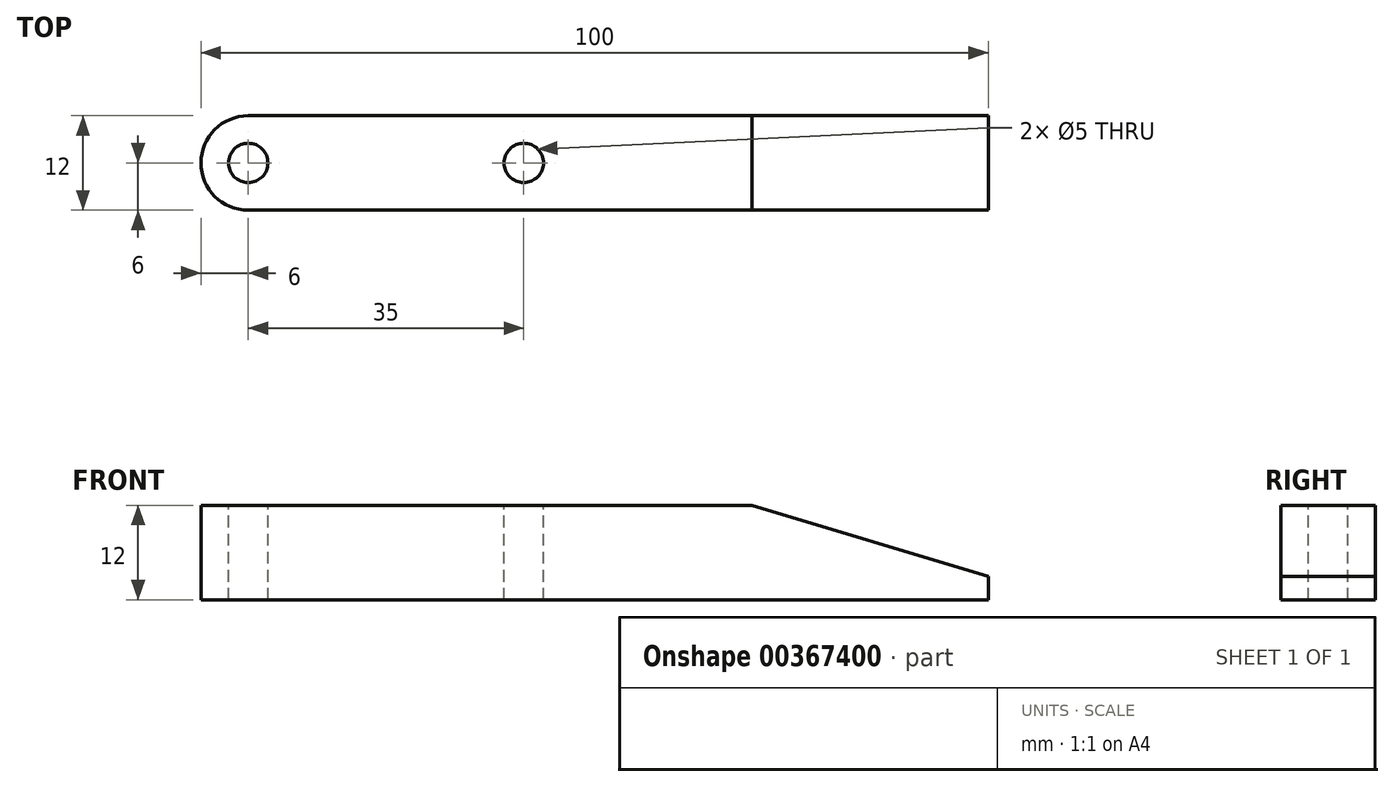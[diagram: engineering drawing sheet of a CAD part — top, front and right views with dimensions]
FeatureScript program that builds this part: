
annotation { "Feature Type Name" : "Feature", "Feature Type Description" : "" }
export const myFeature = defineFeature(function(context is Context, id is Id, definition is map)
    precondition{}
    {
        {
            var Q0;
            Q0=qCreatedBy(makeId("Top.planeOp"),FACE);
            var sketch = newSketch(context, id + "F0", { "sketchPlane" : qUnion([Q0])});
            skLineSegment(sketch, "E0.bottom", {"start": v(0, 0) * mm, "end": v(100, 0) * mm});
            skLineSegment(sketch, "E0.top", {"start": v(0, 12) * mm, "end": v(100, 12) * mm});
            skLineSegment(sketch, "E0.left", {"start": v(0, 0) * mm, "end": v(0, 12) * mm});
            skLineSegment(sketch, "E0.right", {"start": v(100, 0) * mm, "end": v(100, 12) * mm});
            skSolve(sketch);
        }
        {
            var Q0;
            Q0=makeQuery(id+"F0.imprint","IMPRINT",FACE,{"disambiguationData":[TD([[makeQuery(id+"F0.imprint","IMPRINT",EDGE,{"derivedFrom":sQuery(id+"F0.wireOp",EDGE,"E0.bottom")}),1.0]])]});
            extrude(context, id + "F1", {"entities" : qUnion([Q0]), "depth" : 12 * mm});
        }
        {
            var Q0;
            Q0=makeQuery(id+"F1.opExtrude","CAP_EDGE",EDGE,{"disambiguationData":[OSD([sQuery(id+"F0.wireOp",EDGE,"E0.right")])],"isStart":false});
            chamfer(context, id + "F2", {"entities" : qUnion([Q0]), "chamferType" : ChamferType.TWO_OFFSETS, "width1" : 30 * mm, "oppositeDirection" : false, "width2" : 9 * mm, "tangentPropagation" : true});
        }
        {
            var Q0;
            Q0=makeQuery(id+"F1.opExtrude","SWEPT_EDGE",EDGE,{"disambiguationData":[OSD([sQuery(id+"F0.wireOp",EDGE,"E0.bottom"),sQuery(id+"F0.wireOp",EDGE,"E0.left")])]});
            var Q1;
            Q1=makeQuery(id+"F1.opExtrude","SWEPT_EDGE",EDGE,{"disambiguationData":[OSD([sQuery(id+"F0.wireOp",EDGE,"E0.top"),sQuery(id+"F0.wireOp",EDGE,"E0.left")])]});
            fillet(context, id + "F3", {"entities" : qUnion([Q0, Q1]), "radius" : 6 * mm, "tangentPropagation" : true, "allowEdgeOverflow" : false});
        }
        {
            var Q0;
            Q0=makeQuery(id+"F1.opExtrude","CAP_FACE",FACE,{"disambiguationData":[OSD([sQuery(id+"F0.wireOp",EDGE,"E0.bottom"),sQuery(id+"F0.wireOp",EDGE,"E0.top"),sQuery(id+"F0.wireOp",EDGE,"E0.left"),sQuery(id+"F0.wireOp",EDGE,"E0.right")])],"isStart":false});
            var sketch = newSketch(context, id + "F4", { "sketchPlane" : qUnion([Q0])});
            skPoint(sketch, "E1", {"position": v(6, 6) * mm});
            skPoint(sketch, "E2", {"position": v(41, 6) * mm});
            skSolve(sketch);
        }
        {
            var Q0;
            Q0=sQuery(id+"F4.wireOp",VERTEX,"E1");
            var Q1;
            Q1=sQuery(id+"F4.wireOp",VERTEX,"E2");
            var Q2;
            Q2=makeQuery(id+"F1.opExtrude","SWEPT_BODY",BODY,{"disambiguationData":[OSD([sQuery(id+"F0.wireOp",EDGE,"E0.bottom"),sQuery(id+"F0.wireOp",EDGE,"E0.top"),sQuery(id+"F0.wireOp",EDGE,"E0.left"),sQuery(id+"F0.wireOp",EDGE,"E0.right")])]});
            hole(context, id + "F5", {"style" : HoleStyle.SIMPLE, "endStyle" : HoleEndStyle.THROUGH, "standardTappedOrClearance" : lookupTablePath({ "standard" : "ISO", "engagement" : "75%", "pitch" : "1 mm", "size" : "M6", "type" : "Tapped" }), "standardBlindInLast" : lookupTablePath({ "standard" : "ISO", "engagement" : "75%", "pitch" : "1 mm", "size" : "M6", "type" : "Tapped" }), "holeDiameter" : 5 * mm, "showTappedDepth" : true, "isTappedThrough" : true, "tappedDepth" : 12 * mm, "tapClearance" : 3, "locations" : qUnion([Q0, Q1]), "scope" : qUnion([Q2]), "majorDiameter" : 6 * mm});
        }
    });
